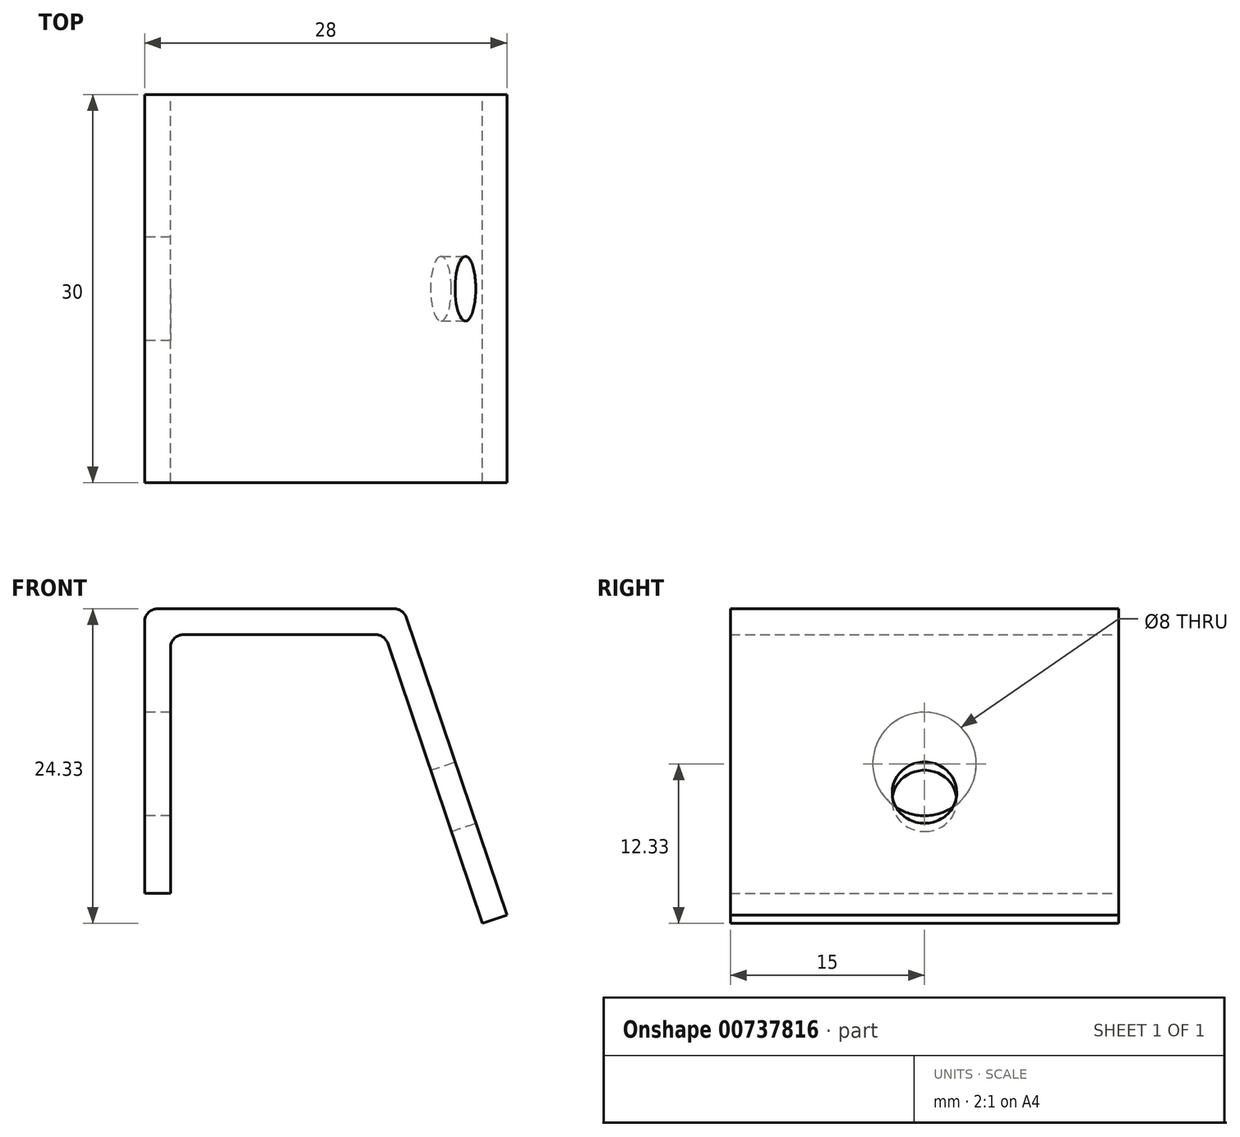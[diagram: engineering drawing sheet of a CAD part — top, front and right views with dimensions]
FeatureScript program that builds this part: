
annotation { "Feature Type Name" : "Feature", "Feature Type Description" : "" }
export const myFeature = defineFeature(function(context is Context, id is Id, definition is map)
    precondition{}
    {
        {
            var Q0;
            Q0=qCreatedBy(makeId("Front.planeOp"),FACE);
            var sketch = newSketch(context, id + "F0", { "sketchPlane" : qUnion([Q0])});
            skLineSegment(sketch, "E0.bottom", {"start": v(10, 11) * mm, "end": v(-10, 11) * mm});
            skLineSegment(sketch, "E0.right", {"start": v(-10, 11) * mm, "end": v(-10, -11) * mm});
            skPoint(sketch, "E0.middle", {"position": v(0, 0) * mm});
            skLineSegment(sketch, "E1", {"start": v(10, 11) * mm, "end": v(18, -12.69) * mm});
            skLineSegment(sketch, "E2.0", {"start": v(-8, 9) * mm, "end": v(-8, -11) * mm});
            skLineSegment(sketch, "E3.0", {"start": v(8.56, 9) * mm, "end": v(-8, 9) * mm});
            skLineSegment(sketch, "E4.0", {"start": v(8.56, 9) * mm, "end": v(16.1, -13.33) * mm});
            skLineSegment(sketch, "E5", {"start": v(-10, -11) * mm, "end": v(-8, -11) * mm});
            skLineSegment(sketch, "E6", {"start": v(16.1, -13.33) * mm, "end": v(18, -12.69) * mm});
            skSolve(sketch);
        }
        {
            var Q0;
            Q0=makeQuery(id+"F0.imprint","IMPRINT",FACE,{"disambiguationData":[TD([[makeQuery(id+"F0.imprint","IMPRINT",EDGE,{"derivedFrom":sQuery(id+"F0.wireOp",EDGE,"E0.bottom")}),1.0]])]});
            extrude(context, id + "F1", {"entities" : qUnion([Q0]), "depth" : 30 * mm, "offsetDistance" : 25 * mm});
        }
        {
            var Q0;
            Q0=makeQuery(id+"F1.opExtrude","SWEPT_EDGE",EDGE,{"disambiguationData":[OSD([sQuery(id+"F0.wireOp",EDGE,"E0.bottom"),sQuery(id+"F0.wireOp",EDGE,"E1")])]});
            var Q1;
            Q1=makeQuery(id+"F1.opExtrude","SWEPT_EDGE",EDGE,{"disambiguationData":[OSD([sQuery(id+"F0.wireOp",EDGE,"E0.bottom"),sQuery(id+"F0.wireOp",EDGE,"E0.right")])]});
            var Q2;
            Q2=makeQuery(id+"F1.opExtrude","SWEPT_EDGE",EDGE,{"disambiguationData":[OSD([sQuery(id+"F0.wireOp",EDGE,"E2.0"),sQuery(id+"F0.wireOp",EDGE,"E3.0")])]});
            var Q3;
            Q3=makeQuery(id+"F1.opExtrude","SWEPT_EDGE",EDGE,{"disambiguationData":[OSD([sQuery(id+"F0.wireOp",EDGE,"E3.0"),sQuery(id+"F0.wireOp",EDGE,"E4.0")])]});
            fillet(context, id + "F2", {"entities" : qUnion([Q0, Q1, Q2, Q3]), "radius" : 1 * mm, "tangentPropagation" : true, "allowEdgeOverflow" : false});
        }
        {
            var Q0;
            Q0=makeQuery(id+"F1.opExtrude","SWEPT_FACE",FACE,{"disambiguationData":[OSD([sQuery(id+"F0.wireOp",EDGE,"E1")])]});
            var sketch = newSketch(context, id + "F3", { "sketchPlane" : qUnion([Q0])});
            skLineSegment(sketch, "E7", {"start": v(-15, -17.78) * mm, "end": v(-15, -7.78) * mm});
            skCircle(sketch, "E8", {"center": v(-15, -7.78) * mm, "radius": 2.5 * mm});
            skSolve(sketch);
        }
        {
            var Q0;
            Q0=makeQuery(id+"F1.opExtrude","SWEPT_FACE",FACE,{"disambiguationData":[OSD([sQuery(id+"F0.wireOp",EDGE,"E0.right")])]});
            var sketch = newSketch(context, id + "F4", { "sketchPlane" : qUnion([Q0])});
            skLineSegment(sketch, "E9", {"start": v(15, -11) * mm, "end": v(15, -1) * mm});
            skCircle(sketch, "E10", {"center": v(15, -1) * mm, "radius": 4 * mm});
            skSolve(sketch);
        }
        {
            var Q0;
            Q0=makeQuery(id+"F3.imprint","IMPRINT",FACE,{"disambiguationData":[TD([[makeQuery(id+"F3.imprint","IMPRINT",EDGE,{"derivedFrom":sQuery(id+"F3.wireOp",EDGE,"E8")}),1.0]])]});
            extrude(context, id + "F5", {"entities" : qUnion([Q0]), "operationType" : NewBodyOperationType.REMOVE, "oppositeDirection" : true, "depth" : 3 * mm, "offsetDistance" : 25 * mm});
        }
        {
            var Q0;
            Q0=makeQuery(id+"F4.imprint","IMPRINT",FACE,{"disambiguationData":[TD([[makeQuery(id+"F4.imprint","IMPRINT",EDGE,{"derivedFrom":sQuery(id+"F4.wireOp",EDGE,"E10")}),1.0]])]});
            extrude(context, id + "F6", {"entities" : qUnion([Q0]), "operationType" : NewBodyOperationType.REMOVE, "oppositeDirection" : true, "depth" : 3 * mm, "offsetDistance" : 25 * mm});
        }
    });
